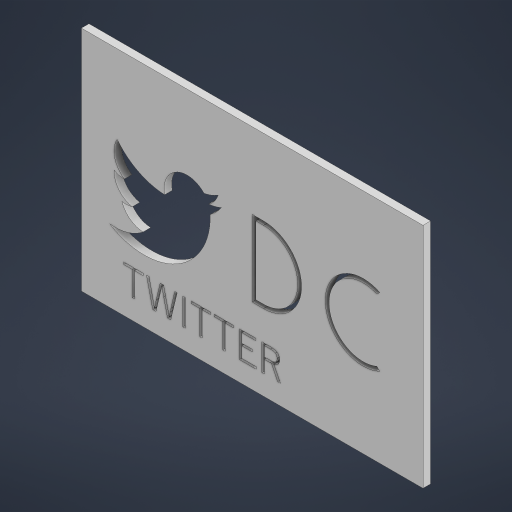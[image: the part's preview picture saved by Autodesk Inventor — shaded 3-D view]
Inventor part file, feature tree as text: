
AUTODESK INVENTOR PART (.ipt)
format: ipt  version: 2023.4 (Build 274418000, 418)  size: 345,088 bytes
history: native  units: mm
features: sketch x3, extrude x2, emboss x1, other x1
ambient origin geometry x8: Origin, YZ Plane, XZ Plane, XY Plane, X Axis, Y Axis, Z Axis, Center Point
bodies: Body1 (feature_tree)
feature tree (7):
  extrude  "Extrusion3"  Depth=300.0mm
  extrude  "Extrusion4"  Depth=10.0mm
  emboss  "Emboss1"
  sketch  "Sketch3"  dims[d28=450.0mm d29=300.0mm]
  sketch  "Sketch4"  dims[d30=10.0mm d31=0.0mm d33=100.0mm]
  other  "Image2"
  sketch  "Sketch5"  dims[d36=50.0mm d37=15.0mm d38=15.0mm d39=5.0mm d41=5.0mm d42=45.0deg d45=0.0mm d46=0.0mm d47=100.0mm d48=0.0mm]
